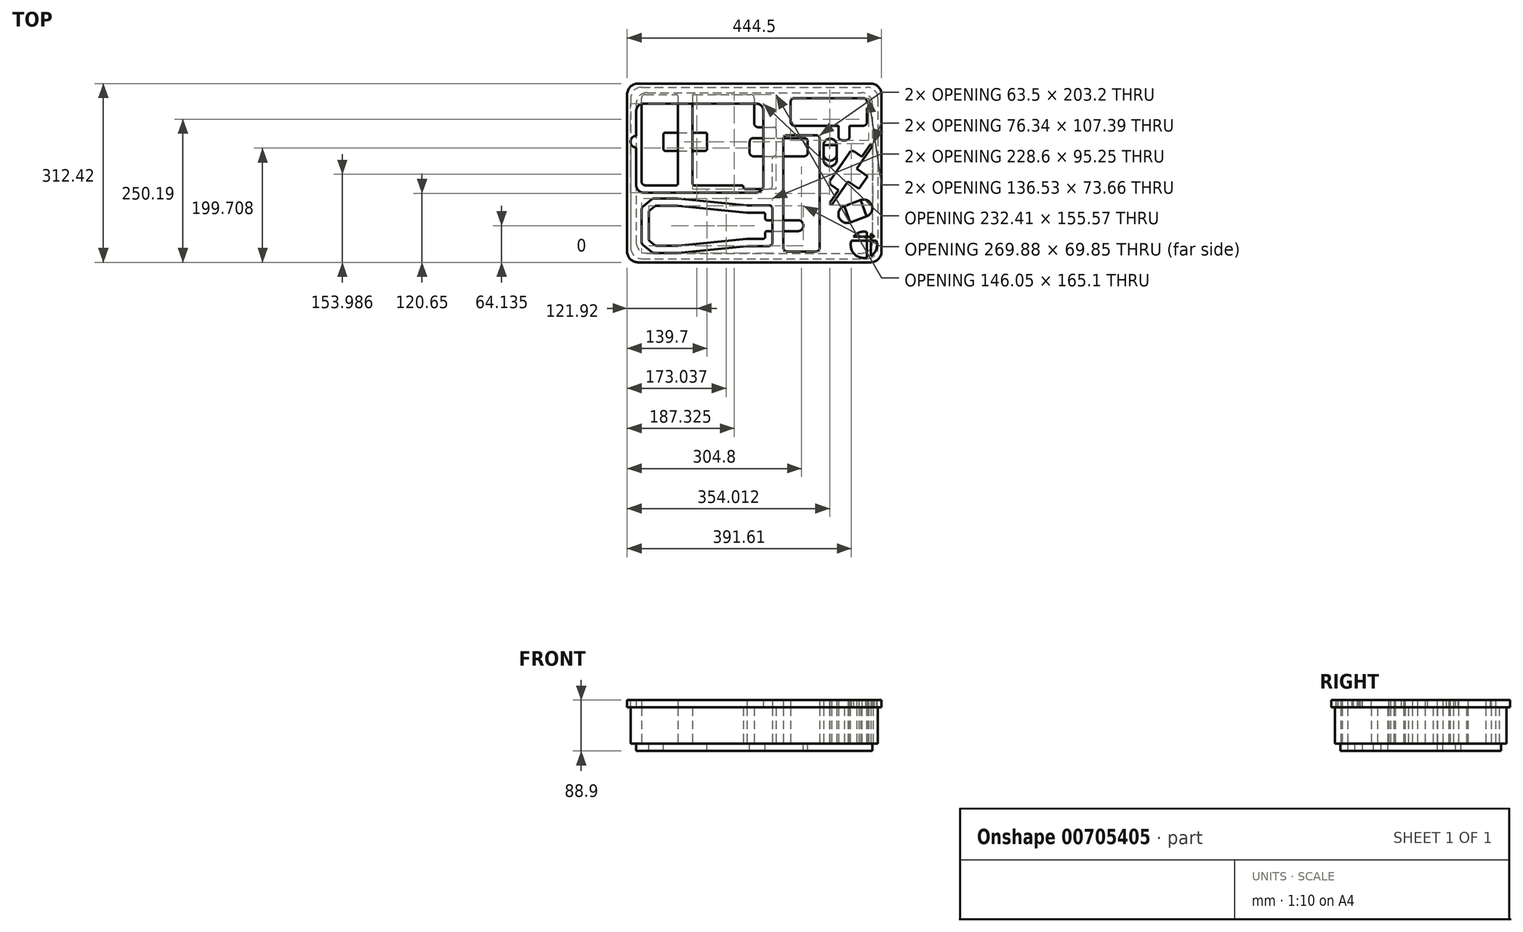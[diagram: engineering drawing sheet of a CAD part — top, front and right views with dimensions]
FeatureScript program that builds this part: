
annotation { "Feature Type Name" : "Feature", "Feature Type Description" : "" }
export const myFeature = defineFeature(function(context is Context, id is Id, definition is map)
    precondition{}
    {
        {
            var Q0;
            Q0=qCreatedBy(makeId("Top.planeOp"),FACE);
            var sketch = newSketch(context, id + "F0", { "sketchPlane" : qUnion([Q0])});
            skLineSegment(sketch, "E0.bottom", {"start": v(-196.85, 149.86) * mm, "end": v(196.85, 149.86) * mm});
            skLineSegment(sketch, "E0.top", {"start": v(-196.85, -149.86) * mm, "end": v(196.85, -149.86) * mm});
            skLineSegment(sketch, "E0.left", {"start": v(-215.9, 130.81) * mm, "end": v(-215.9, -130.81) * mm});
            skLineSegment(sketch, "E0.right", {"start": v(215.9, 130.81) * mm, "end": v(215.9, -130.8) * mm});
            skLineSegment(sketch, "E1.bottom", {"start": v(-196.85, -15.24) * mm, "end": v(-196.85, 130.81) * mm});
            skLineSegment(sketch, "E1.top", {"start": v(31.75, -21.59) * mm, "end": v(31.75, 26.04) * mm});
            skLineSegment(sketch, "E1.right", {"start": v(-190.5, 137.16) * mm, "end": v(-136.52, 137.16) * mm});
            skLineSegment(sketch, "E2.bottom", {"start": v(157, -57.85) * mm, "end": v(185.64, -47.43) * mm});
            skLineSegment(sketch, "E2.top", {"start": v(167.42, -86.5) * mm, "end": v(196.06, -76.07) * mm});
            skLineSegment(sketch, "E2.left", {"start": v(157, -57.85) * mm, "end": v(167.42, -86.5) * mm});
            skLineSegment(sketch, "E2.right", {"start": v(185.64, -47.43) * mm, "end": v(196.06, -76.07) * mm});
            skLineSegment(sketch, "E3", {"start": v(149.5, 11.49) * mm, "end": v(190.26, -16.66) * mm, "construction": true});
            skLineSegment(sketch, "E4", {"start": v(149.5, 11.49) * mm, "end": v(132.9, -12.55) * mm});
            skLineSegment(sketch, "E5", {"start": v(134.52, -21.38) * mm, "end": v(147.06, -30.04) * mm});
            skLineSegment(sketch, "E6", {"start": v(147.06, -30.04) * mm, "end": v(131.19, -53.04) * mm});
            skLineSegment(sketch, "E7", {"start": v(131.19, -53.04) * mm, "end": v(135.37, -55.92) * mm});
            skLineSegment(sketch, "E8", {"start": v(179.03, 7.3) * mm, "end": v(197.84, -5.68) * mm});
            skLineSegment(sketch, "E9", {"start": v(197.84, -5.68) * mm, "end": v(190.26, -16.66) * mm});
            skPoint(sketch, "E10.visualSharp", {"position": v(129.3, -17.78) * mm});
            skArc(sketch, "E10.filletArc", {"start": v(132.9, -12.55) * mm, "mid": v(131.89, -17.3) * mm, "end": v(134.52, -21.38) * mm});
            skArc(sketch, "E11.MirrorCS", {"start": v(166.1, 35.52) * mm, "mid": v(170.18, 38.16) * mm, "end": v(174.93, 37.14) * mm});
            skLineSegment(sketch, "E12.MirrorCS", {"start": v(187.47, 28.48) * mm, "end": v(203.35, 51.47) * mm});
            skLineSegment(sketch, "E13.MirrorCS", {"start": v(174.93, 37.14) * mm, "end": v(187.47, 28.48) * mm});
            skPoint(sketch, "E14.MirrorP", {"position": v(169.7, 40.75) * mm});
            skLineSegment(sketch, "E15.MirrorCS", {"start": v(163.87, -14.64) * mm, "end": v(182.68, -27.63) * mm});
            skLineSegment(sketch, "E16.MirrorCS", {"start": v(149.5, 11.49) * mm, "end": v(166.1, 35.52) * mm});
            skLineSegment(sketch, "E17.MirrorCS", {"start": v(182.68, -27.63) * mm, "end": v(190.26, -16.66) * mm});
            skLineSegment(sketch, "E18", {"start": v(163.87, -14.64) * mm, "end": v(135.37, -55.92) * mm});
            skPoint(sketch, "E19.visualSharp", {"position": v(-215.9, 149.86) * mm});
            skArc(sketch, "E19.filletArc", {"start": v(-196.85, 149.86) * mm, "mid": v(-210.32, 144.28) * mm, "end": v(-215.9, 130.81) * mm});
            skPoint(sketch, "E20.visualSharp", {"position": v(215.9, 149.86) * mm});
            skArc(sketch, "E20.filletArc", {"start": v(215.9, 130.81) * mm, "mid": v(210.32, 144.28) * mm, "end": v(196.85, 149.86) * mm});
            skPoint(sketch, "E21.visualSharp", {"position": v(215.9, -149.86) * mm});
            skArc(sketch, "E21.filletArc", {"start": v(196.85, -149.86) * mm, "mid": v(210.32, -144.28) * mm, "end": v(215.9, -130.8) * mm});
            skPoint(sketch, "E22.visualSharp", {"position": v(-215.9, -149.86) * mm});
            skArc(sketch, "E22.filletArc", {"start": v(-215.9, -130.81) * mm, "mid": v(-210.32, -144.28) * mm, "end": v(-196.85, -149.86) * mm});
            skPoint(sketch, "E23.visualSharp", {"position": v(-196.85, -27.94) * mm});
            skPoint(sketch, "E24.visualSharp", {"position": v(31.75, -27.94) * mm});
            skArc(sketch, "E24.filletArc", {"start": v(25.4, -27.94) * mm, "mid": v(29.9, -26.08) * mm, "end": v(31.75, -21.59) * mm});
            skPoint(sketch, "E25.visualSharp", {"position": v(-196.85, 137.16) * mm});
            skArc(sketch, "E25.filletArc", {"start": v(-190.5, 137.16) * mm, "mid": v(-195, 135.3) * mm, "end": v(-196.85, 130.81) * mm});
            skPoint(sketch, "E26.visualSharp", {"position": v(31.75, 137.16) * mm});
            skArc(sketch, "E26.filletArc", {"start": v(31.75, 130.81) * mm, "mid": v(29.9, 135.3) * mm, "end": v(25.4, 137.16) * mm, "construction": true});
            skLineSegment(sketch, "E27.bottom", {"start": v(63.5, 88.9) * mm, "end": v(63.5, 124.46) * mm});
            skLineSegment(sketch, "E27.top", {"start": v(196.85, 88.9) * mm, "end": v(196.85, 112.08) * mm});
            skLineSegment(sketch, "E27.left", {"start": v(69.85, 82.55) * mm, "end": v(146.05, 82.55) * mm});
            skLineSegment(sketch, "E27.right", {"start": v(69.85, 130.81) * mm, "end": v(190.5, 130.81) * mm});
            skLineSegment(sketch, "E28.bottom", {"start": v(147.32, 81.28) * mm, "end": v(147.32, 63.5) * mm});
            skLineSegment(sketch, "E28.top", {"start": v(166.37, 81.28) * mm, "end": v(166.37, 63.5) * mm});
            skLineSegment(sketch, "E28.right", {"start": v(153.67, 57.15) * mm, "end": v(160.02, 57.15) * mm});
            skLineSegment(sketch, "E29.trimOffspring", {"start": v(167.64, 82.55) * mm, "end": v(190.5, 82.55) * mm});
            skLineSegment(sketch, "E30", {"start": v(147.32, 82.55) * mm, "end": v(166.37, 82.55) * mm, "construction": true});
            skPoint(sketch, "E31.visualSharp", {"position": v(63.5, 82.55) * mm});
            skArc(sketch, "E31.filletArc", {"start": v(63.5, 88.9) * mm, "mid": v(65.36, 84.4) * mm, "end": v(69.85, 82.55) * mm});
            skPoint(sketch, "E32.visualSharp", {"position": v(196.85, 82.55) * mm});
            skArc(sketch, "E32.filletArc", {"start": v(190.5, 82.55) * mm, "mid": v(195, 84.4) * mm, "end": v(196.85, 88.9) * mm});
            skArc(sketch, "E33.filletArc", {"start": v(196.85, 124.46) * mm, "mid": v(195, 128.95) * mm, "end": v(190.5, 130.81) * mm});
            skPoint(sketch, "E34.visualSharp", {"position": v(63.5, 130.81) * mm});
            skArc(sketch, "E34.filletArc", {"start": v(69.85, 130.81) * mm, "mid": v(65.36, 128.95) * mm, "end": v(63.5, 124.46) * mm});
            skPoint(sketch, "E35.visualSharp", {"position": v(147.32, 57.15) * mm});
            skArc(sketch, "E35.filletArc", {"start": v(147.32, 63.5) * mm, "mid": v(149.18, 59) * mm, "end": v(153.67, 57.15) * mm});
            skPoint(sketch, "E36.visualSharp", {"position": v(166.37, 57.15) * mm});
            skArc(sketch, "E36.filletArc", {"start": v(160.02, 57.15) * mm, "mid": v(164.51, 59) * mm, "end": v(166.37, 63.5) * mm});
            skLineSegment(sketch, "E37.bottom", {"start": v(120.85, 48.4) * mm, "end": v(143.96, 48.4) * mm});
            skLineSegment(sketch, "E37.left", {"start": v(120.85, 48.4) * mm, "end": v(120.85, 33.17) * mm});
            skLineSegment(sketch, "E37.right", {"start": v(143.96, 48.4) * mm, "end": v(143.96, 33.17) * mm});
            skArc(sketch, "E38", {"start": v(120.85, 33.17) * mm, "mid": v(132.4, 21.6) * mm, "end": v(143.96, 33.17) * mm});
            skLineSegment(sketch, "E39.bottom", {"start": v(-196.85, -139.7) * mm, "end": v(-196.85, -44.45) * mm, "construction": true});
            skLineSegment(sketch, "E39.top", {"start": v(31.75, -139.7) * mm, "end": v(31.75, -44.45) * mm, "construction": true});
            skLineSegment(sketch, "E39.left", {"start": v(-196.85, -139.7) * mm, "end": v(31.75, -139.7) * mm, "construction": true});
            skLineSegment(sketch, "E39.right", {"start": v(-196.85, -44.45) * mm, "end": v(31.75, -44.45) * mm, "construction": true});
            skLineSegment(sketch, "E40", {"start": v(-196.85, -92.08) * mm, "end": v(31.75, -92.07) * mm, "construction": true});
            skLineSegment(sketch, "E41", {"start": v(-196.85, -123.83) * mm, "end": v(31.75, -123.82) * mm, "construction": true});
            skLineSegment(sketch, "E42.MirrorCS", {"start": v(-196.85, -60.33) * mm, "end": v(31.75, -60.32) * mm, "construction": true});
            skLineSegment(sketch, "E43", {"start": v(-196.85, -127.64) * mm, "end": v(31.75, -127.63) * mm, "construction": true});
            skLineSegment(sketch, "E44.MirrorCS", {"start": v(-196.85, -56.51) * mm, "end": v(31.75, -56.51) * mm, "construction": true});
            skLineSegment(sketch, "E45", {"start": v(-177.16, -139.7) * mm, "end": v(-177.16, -44.45) * mm, "construction": true});
            skLineSegment(sketch, "E46", {"start": v(-133.35, -139.7) * mm, "end": v(-133.35, -44.45) * mm, "construction": true});
            skLineSegment(sketch, "E47", {"start": v(-12.7, -139.7) * mm, "end": v(-12.7, -44.45) * mm, "construction": true});
            skLineSegment(sketch, "E48", {"start": v(-196.85, -120.79) * mm, "end": v(-196.85, -63.36) * mm});
            skLineSegment(sketch, "E49", {"start": v(-194.49, -58.42) * mm, "end": v(-178.9, -45.86) * mm});
            skLineSegment(sketch, "E50", {"start": v(-174.92, -44.45) * mm, "end": v(-133.35, -44.45) * mm});
            skLineSegment(sketch, "E51", {"start": v(-133.35, -44.45) * mm, "end": v(-12.7, -56.51) * mm});
            skLineSegment(sketch, "E52", {"start": v(-12.7, -56.51) * mm, "end": v(25.4, -56.51) * mm});
            skLineSegment(sketch, "E53", {"start": v(31.75, -62.86) * mm, "end": v(31.75, -121.28) * mm});
            skLineSegment(sketch, "E54", {"start": v(25.4, -127.63) * mm, "end": v(-12.7, -127.63) * mm});
            skLineSegment(sketch, "E55", {"start": v(-12.7, -127.64) * mm, "end": v(-133.35, -139.7) * mm});
            skLineSegment(sketch, "E56", {"start": v(-133.35, -139.7) * mm, "end": v(-174.92, -139.7) * mm});
            skLineSegment(sketch, "E57", {"start": v(-178.9, -138.3) * mm, "end": v(-194.49, -125.73) * mm});
            skPoint(sketch, "E58.visualSharp", {"position": v(31.75, -127.64) * mm});
            skArc(sketch, "E58.filletArc", {"start": v(25.4, -127.63) * mm, "mid": v(29.9, -125.78) * mm, "end": v(31.75, -121.28) * mm});
            skPoint(sketch, "E59.visualSharp", {"position": v(31.75, -56.51) * mm});
            skArc(sketch, "E59.filletArc", {"start": v(31.75, -62.86) * mm, "mid": v(29.9, -58.37) * mm, "end": v(25.4, -56.51) * mm});
            skPoint(sketch, "E60.visualSharp", {"position": v(-196.85, -123.83) * mm});
            skArc(sketch, "E60.filletArc", {"start": v(-196.85, -120.79) * mm, "mid": v(-196.23, -123.53) * mm, "end": v(-194.49, -125.73) * mm});
            skPoint(sketch, "E61.visualSharp", {"position": v(-177.16, -139.7) * mm});
            skArc(sketch, "E61.filletArc", {"start": v(-178.9, -138.3) * mm, "mid": v(-177.04, -139.34) * mm, "end": v(-174.92, -139.7) * mm});
            skPoint(sketch, "E62.visualSharp", {"position": v(-196.85, -60.33) * mm});
            skArc(sketch, "E62.filletArc", {"start": v(-194.49, -58.42) * mm, "mid": v(-196.23, -60.62) * mm, "end": v(-196.85, -63.36) * mm});
            skPoint(sketch, "E63.visualSharp", {"position": v(-177.16, -44.45) * mm});
            skArc(sketch, "E63.filletArc", {"start": v(-174.92, -44.45) * mm, "mid": v(-177.04, -44.81) * mm, "end": v(-178.9, -45.86) * mm});
            skLineSegment(sketch, "E64", {"start": v(120.85, 33.17) * mm, "end": v(143.96, 33.17) * mm, "construction": true});
            skLineSegment(sketch, "E65.MirrorCS", {"start": v(179.03, 7.3) * mm, "end": v(207.53, 48.59) * mm});
            skLineSegment(sketch, "E66.MirrorCS", {"start": v(203.35, 51.47) * mm, "end": v(207.53, 48.59) * mm});
            skLineSegment(sketch, "E67", {"start": v(198.12, 122.87) * mm, "end": v(198.76, 122.87) * mm});
            skLineSegment(sketch, "E68", {"start": v(200.02, 121.6) * mm, "end": v(200.02, 114.62) * mm});
            skLineSegment(sketch, "E69", {"start": v(198.76, 113.35) * mm, "end": v(198.12, 113.35) * mm});
            skPoint(sketch, "E70.visualSharp", {"position": v(166.37, 82.55) * mm});
            skArc(sketch, "E70.filletArc", {"start": v(167.64, 82.55) * mm, "mid": v(166.74, 82.18) * mm, "end": v(166.37, 81.28) * mm});
            skPoint(sketch, "E71.visualSharp", {"position": v(147.32, 82.55) * mm});
            skArc(sketch, "E71.filletArc", {"start": v(147.32, 81.28) * mm, "mid": v(146.95, 82.18) * mm, "end": v(146.05, 82.55) * mm});
            skPoint(sketch, "E72.visualSharp", {"position": v(200.03, 113.35) * mm});
            skArc(sketch, "E72.filletArc", {"start": v(198.76, 113.35) * mm, "mid": v(199.65, 113.72) * mm, "end": v(200.03, 114.62) * mm});
            skPoint(sketch, "E73.visualSharp", {"position": v(200.03, 122.87) * mm});
            skArc(sketch, "E73.filletArc", {"start": v(200.02, 121.6) * mm, "mid": v(199.65, 122.5) * mm, "end": v(198.76, 122.87) * mm});
            skPoint(sketch, "E74.visualSharp", {"position": v(196.85, 122.87) * mm});
            skArc(sketch, "E74.filletArc", {"start": v(196.85, 124.13) * mm, "mid": v(197.23, 123.24) * mm, "end": v(198.12, 122.87) * mm});
            skPoint(sketch, "E75.visualSharp", {"position": v(196.85, 113.35) * mm});
            skArc(sketch, "E75.filletArc", {"start": v(198.12, 113.35) * mm, "mid": v(197.22, 112.98) * mm, "end": v(196.85, 112.08) * mm});
            skLineSegment(sketch, "E76", {"start": v(-196.85, 54.61) * mm, "end": v(31.75, 54.61) * mm, "construction": true});
            skLineSegment(sketch, "E77", {"start": v(-82.55, -27.94) * mm, "end": v(-82.55, 137.16) * mm, "construction": true});
            skLineSegment(sketch, "E78", {"start": v(0, 149.86) * mm, "end": v(0, -149.86) * mm, "construction": true});
            skLineSegment(sketch, "E79", {"start": v(-215.9, 0) * mm, "end": v(215.9, 0) * mm, "construction": true});
            skPoint(sketch, "E80", {"position": v(0, 0) * mm});
            skPoint(sketch, "E81", {"position": v(-82.55, 54.61) * mm});
            skPoint(sketch, "E82", {"position": v(-133.35, -92.08) * mm});
            skLineSegment(sketch, "E83", {"start": v(63.5, 106.68) * mm, "end": v(196.85, 106.68) * mm, "construction": true});
            skLineSegment(sketch, "E84", {"start": v(130.18, 130.81) * mm, "end": v(130.18, 82.55) * mm, "construction": true});
            skPoint(sketch, "E85", {"position": v(130.18, 106.68) * mm});
            skLineSegment(sketch, "E86", {"start": v(163.87, -14.64) * mm, "end": v(179.03, 7.3) * mm, "construction": true});
            skPoint(sketch, "E87", {"position": v(171.45, -3.67) * mm});
            skLineSegment(sketch, "E88", {"start": v(196.85, 124.46) * mm, "end": v(196.85, 124.13) * mm});
            skLineSegment(sketch, "E89", {"start": v(196.85, 124.13) * mm, "end": v(196.85, 112.08) * mm, "construction": true});
            skArc(sketch, "E90", {"start": v(31.75, -21.59) * mm, "mid": v(29.9, -26.08) * mm, "end": v(25.4, -27.94) * mm});
            skLineSegment(sketch, "E91.bottom", {"start": v(107.95, -137.16) * mm, "end": v(57.15, -137.16) * mm});
            skLineSegment(sketch, "E91.top", {"start": v(107.95, 66.04) * mm, "end": v(57.15, 66.04) * mm});
            skLineSegment(sketch, "E91.left", {"start": v(114.3, -130.8) * mm, "end": v(114.3, 59.7) * mm});
            skLineSegment(sketch, "E91.right", {"start": v(50.8, -130.8) * mm, "end": v(50.8, 59.7) * mm});
            skLineSegment(sketch, "E92", {"start": v(82.55, -137.16) * mm, "end": v(82.55, 66.04) * mm, "construction": true});
            skLineSegment(sketch, "E93", {"start": v(114.3, -35.56) * mm, "end": v(50.8, -35.56) * mm, "construction": true});
            skPoint(sketch, "E94", {"position": v(82.55, -35.56) * mm});
            skPoint(sketch, "E95.visualSharp", {"position": v(114.3, -137.16) * mm});
            skArc(sketch, "E95.filletArc", {"start": v(107.95, -137.16) * mm, "mid": v(112.44, -135.3) * mm, "end": v(114.3, -130.8) * mm});
            skPoint(sketch, "E96.visualSharp", {"position": v(50.8, -137.16) * mm});
            skArc(sketch, "E96.filletArc", {"start": v(50.8, -130.8) * mm, "mid": v(52.66, -135.3) * mm, "end": v(57.15, -137.16) * mm});
            skPoint(sketch, "E97.visualSharp", {"position": v(50.8, 66.04) * mm});
            skArc(sketch, "E97.filletArc", {"start": v(57.15, 66.04) * mm, "mid": v(52.66, 64.18) * mm, "end": v(50.8, 59.7) * mm});
            skPoint(sketch, "E98.visualSharp", {"position": v(114.3, 66.04) * mm});
            skArc(sketch, "E98.filletArc", {"start": v(114.3, 59.7) * mm, "mid": v(112.44, 64.18) * mm, "end": v(107.95, 66.04) * mm});
            skLineSegment(sketch, "E99.left", {"start": v(-107.95, 133.99) * mm, "end": v(-107.95, -18.41) * mm});
            skLineSegment(sketch, "E99.right", {"start": v(-133.35, 133.99) * mm, "end": v(-133.35, -18.41) * mm});
            skLineSegment(sketch, "E100", {"start": v(34.93, 80.01) * mm, "end": v(34.92, 80.01) * mm});
            skLineSegment(sketch, "E101.MirrorCS", {"start": v(34.93, 29.21) * mm, "end": v(34.93, 29.21) * mm});
            skLineSegment(sketch, "E102", {"start": v(38.1, 76.84) * mm, "end": v(38.1, 32.39) * mm});
            skLineSegment(sketch, "E103", {"start": v(-104.77, 137.16) * mm, "end": v(-6.35, 137.16) * mm});
            skLineSegment(sketch, "E104", {"start": v(31.75, 83.19) * mm, "end": v(31.75, 130.81) * mm, "construction": true});
            skLineSegment(sketch, "E105", {"start": v(31.75, 29.21) * mm, "end": v(31.75, 80.01) * mm, "construction": true});
            skPoint(sketch, "E106.visualSharp", {"position": v(-107.95, 137.16) * mm});
            skArc(sketch, "E106.filletArc", {"start": v(-104.77, 137.16) * mm, "mid": v(-107.02, 136.23) * mm, "end": v(-107.95, 133.99) * mm});
            skPoint(sketch, "E107.visualSharp", {"position": v(-133.35, 137.16) * mm});
            skArc(sketch, "E107.filletArc", {"start": v(-133.35, 133.99) * mm, "mid": v(-134.28, 136.23) * mm, "end": v(-136.52, 137.16) * mm});
            skPoint(sketch, "E108.visualSharp", {"position": v(31.75, 80.01) * mm});
            skPoint(sketch, "E109.visualSharp", {"position": v(31.75, 29.21) * mm});
            skArc(sketch, "E109.filletArc", {"start": v(34.93, 29.21) * mm, "mid": v(32.68, 28.28) * mm, "end": v(31.75, 26.04) * mm});
            skPoint(sketch, "E110.visualSharp", {"position": v(38.1, 29.21) * mm});
            skArc(sketch, "E110.filletArc", {"start": v(34.93, 29.21) * mm, "mid": v(37.17, 30.14) * mm, "end": v(38.1, 32.39) * mm});
            skPoint(sketch, "E111.visualSharp", {"position": v(38.1, 80.01) * mm});
            skArc(sketch, "E111.filletArc", {"start": v(38.1, 76.84) * mm, "mid": v(37.17, 79.08) * mm, "end": v(34.92, 80.01) * mm});
            skLineSegment(sketch, "E112", {"start": v(0, 130.81) * mm, "end": v(0, 86.36) * mm});
            skLineSegment(sketch, "E113", {"start": v(6.35, 80.01) * mm, "end": v(34.93, 80.01) * mm});
            skPoint(sketch, "E114.visualSharp", {"position": v(0, 80.01) * mm});
            skArc(sketch, "E114.filletArc", {"start": v(0, 86.36) * mm, "mid": v(1.86, 81.87) * mm, "end": v(6.35, 80.01) * mm});
            skLineSegment(sketch, "E115", {"start": v(-6.35, 137.16) * mm, "end": v(0, 137.16) * mm, "construction": true});
            skLineSegment(sketch, "E116", {"start": v(0, 137.16) * mm, "end": v(25.4, 137.16) * mm, "construction": true});
            skPoint(sketch, "E117.visualSharp", {"position": v(0, 137.16) * mm});
            skArc(sketch, "E117.filletArc", {"start": v(0, 130.81) * mm, "mid": v(-1.86, 135.3) * mm, "end": v(-6.35, 137.16) * mm});
            skLineSegment(sketch, "E118", {"start": v(-6.35, 137.16) * mm, "end": v(-6.35, 137.16) * mm});
            skLineSegment(sketch, "E119", {"start": v(-19.05, -24.76) * mm, "end": v(-19.05, -24.76) * mm});
            skLineSegment(sketch, "E120", {"start": v(-22.22, -21.59) * mm, "end": v(-104.78, -21.59) * mm});
            skLineSegment(sketch, "E121", {"start": v(-133.35, -21.59) * mm, "end": v(-133.35, -24.76) * mm, "construction": true});
            skLineSegment(sketch, "E122", {"start": v(-15.88, -27.94) * mm, "end": v(25.4, -27.94) * mm});
            skLineSegment(sketch, "E123", {"start": v(-107.95, -21.59) * mm, "end": v(-107.95, -24.76) * mm, "construction": true});
            skPoint(sketch, "E124.visualSharp", {"position": v(-196.85, -21.59) * mm});
            skArc(sketch, "E124.filletArc", {"start": v(-196.85, -15.24) * mm, "mid": v(-195, -19.73) * mm, "end": v(-190.5, -21.59) * mm});
            skPoint(sketch, "E125.visualSharp", {"position": v(-19.05, -21.59) * mm});
            skArc(sketch, "E125.filletArc", {"start": v(-19.05, -24.76) * mm, "mid": v(-19.98, -22.52) * mm, "end": v(-22.22, -21.59) * mm});
            skPoint(sketch, "E126.visualSharp", {"position": v(-19.05, -27.94) * mm});
            skArc(sketch, "E126.filletArc", {"start": v(-19.05, -24.76) * mm, "mid": v(-18.12, -27.01) * mm, "end": v(-15.88, -27.94) * mm});
            skLineSegment(sketch, "E127", {"start": v(-136.53, -21.59) * mm, "end": v(-190.5, -21.59) * mm});
            skPoint(sketch, "E128.visualSharp", {"position": v(-133.35, -21.59) * mm});
            skArc(sketch, "E128.filletArc", {"start": v(-136.53, -21.59) * mm, "mid": v(-134.28, -20.66) * mm, "end": v(-133.35, -18.41) * mm});
            skPoint(sketch, "E129.visualSharp", {"position": v(-107.95, -21.59) * mm});
            skArc(sketch, "E129.filletArc", {"start": v(-107.95, -18.41) * mm, "mid": v(-107.02, -20.66) * mm, "end": v(-104.78, -21.59) * mm});
            skLineSegment(sketch, "E130", {"start": v(-136.53, -21.59) * mm, "end": v(-104.78, -21.59) * mm, "construction": true});
            skLineSegment(sketch, "E131", {"start": v(-136.52, 137.16) * mm, "end": v(-104.77, 137.16) * mm, "construction": true});
            skSolve(sketch);
        }
        {
            var Q0;
            Q0=qSketchRegion(id+"F0",true);
            extrude(context, id + "F1", {"entities" : qUnion([Q0]), "depth" : 63.5 * mm, "offsetDistance" : 25.4 * mm});
        }
        {
            var Q0;
            Q0=qCreatedBy(makeId("Top.planeOp"),FACE);
            var sketch = newSketch(context, id + "F2", { "sketchPlane" : qUnion([Q0])});
            skLineSegment(sketch, "E132.0", {"start": v(-215.9, 149.86) * mm, "end": v(215.9, 149.86) * mm, "construction": true});
            skLineSegment(sketch, "E133.0", {"start": v(-215.9, 149.86) * mm, "end": v(-215.9, -149.86) * mm, "construction": true});
            skLineSegment(sketch, "E134.0", {"start": v(215.9, 149.86) * mm, "end": v(215.9, -149.86) * mm, "construction": true});
            skLineSegment(sketch, "E135.0", {"start": v(-190.26, -149.86) * mm, "end": v(215.9, -149.86) * mm, "construction": true});
            skPoint(sketch, "E136.orphan", {"position": v(-196.85, 149.86) * mm});
            skPoint(sketch, "E137.orphan", {"position": v(-215.9, 130.81) * mm});
            skPoint(sketch, "E138.orphan", {"position": v(196.85, 149.86) * mm});
            skPoint(sketch, "E139.orphan", {"position": v(215.9, 130.81) * mm});
            skPoint(sketch, "E140.orphan", {"position": v(215.9, -130.8) * mm});
            skPoint(sketch, "E141.orphan", {"position": v(196.85, -149.86) * mm});
            skPoint(sketch, "E142.orphan", {"position": v(-196.85, -149.86) * mm});
            skPoint(sketch, "E143.orphan", {"position": v(-215.9, -130.81) * mm});
            skPoint(sketch, "E144", {"position": v(0, 0) * mm});
            skLineSegment(sketch, "E145", {"start": v(0, 149.86) * mm, "end": v(0, -149.86) * mm, "construction": true});
            skPoint(sketch, "E145.startSnap0", {"position": v(0, 149.86) * mm});
            skLineSegment(sketch, "E146", {"start": v(-215.9, 0) * mm, "end": v(215.9, 0) * mm, "construction": true});
            skLineSegment(sketch, "E147.bottom", {"start": v(-187.32, 140.34) * mm, "end": v(187.33, 140.34) * mm});
            skLineSegment(sketch, "E147.top", {"start": v(-187.33, -140.33) * mm, "end": v(187.32, -140.33) * mm});
            skLineSegment(sketch, "E147.left", {"start": v(-206.38, 121.29) * mm, "end": v(-206.38, -121.28) * mm});
            skLineSegment(sketch, "E147.right", {"start": v(206.38, 121.29) * mm, "end": v(206.38, -121.28) * mm});
            skPoint(sketch, "E148.visualSharp", {"position": v(-206.38, 140.34) * mm});
            skPoint(sketch, "E149.visualSharp", {"position": v(206.38, 140.34) * mm});
            skPoint(sketch, "E150.visualSharp", {"position": v(206.38, -140.33) * mm});
            skPoint(sketch, "E151.visualSharp", {"position": v(-206.38, -140.33) * mm});
            skLineSegment(sketch, "E152.0.0", {"start": v(-12.7, -127.63) * mm, "end": v(25.4, -127.63) * mm, "construction": true});
            skArc(sketch, "E152.0.1", {"start": v(25.4, -127.63) * mm, "mid": v(29.9, -125.78) * mm, "end": v(31.75, -121.28) * mm, "construction": true});
            skLineSegment(sketch, "E152.0.2", {"start": v(31.75, -121.28) * mm, "end": v(31.75, -62.86) * mm, "construction": true});
            skArc(sketch, "E152.0.3", {"start": v(31.75, -62.86) * mm, "mid": v(29.9, -58.37) * mm, "end": v(25.4, -56.51) * mm, "construction": true});
            skLineSegment(sketch, "E152.0.4", {"start": v(25.4, -56.51) * mm, "end": v(-12.7, -56.51) * mm, "construction": true});
            skLineSegment(sketch, "E152.0.5", {"start": v(-12.7, -56.52) * mm, "end": v(-133.35, -44.45) * mm, "construction": true});
            skLineSegment(sketch, "E152.0.6", {"start": v(-133.35, -44.45) * mm, "end": v(-174.92, -44.45) * mm, "construction": true});
            skArc(sketch, "E152.0.7", {"start": v(-174.92, -44.45) * mm, "mid": v(-177.04, -44.81) * mm, "end": v(-178.9, -45.86) * mm, "construction": true});
            skLineSegment(sketch, "E152.0.8", {"start": v(-178.9, -45.86) * mm, "end": v(-194.49, -58.42) * mm, "construction": true});
            skArc(sketch, "E152.0.9", {"start": v(-194.49, -58.42) * mm, "mid": v(-196.23, -60.62) * mm, "end": v(-196.85, -63.36) * mm, "construction": true});
            skLineSegment(sketch, "E152.0.10", {"start": v(-196.85, -63.36) * mm, "end": v(-196.85, -120.79) * mm, "construction": true});
            skArc(sketch, "E152.0.11", {"start": v(-196.85, -120.79) * mm, "mid": v(-196.23, -123.53) * mm, "end": v(-194.49, -125.73) * mm, "construction": true});
            skLineSegment(sketch, "E152.0.12", {"start": v(-194.49, -125.73) * mm, "end": v(-178.9, -138.3) * mm, "construction": true});
            skArc(sketch, "E152.0.13", {"start": v(-178.9, -138.3) * mm, "mid": v(-177.04, -139.34) * mm, "end": v(-174.92, -139.7) * mm, "construction": true});
            skLineSegment(sketch, "E152.0.14", {"start": v(-174.92, -139.7) * mm, "end": v(-133.35, -139.7) * mm, "construction": true});
            skLineSegment(sketch, "E152.0.15", {"start": v(-133.35, -139.7) * mm, "end": v(-12.7, -127.64) * mm, "construction": true});
            skArc(sketch, "E153.filletArc", {"start": v(-187.32, 140.34) * mm, "mid": v(-200.8, 134.76) * mm, "end": v(-206.38, 121.29) * mm});
            skArc(sketch, "E154.filletArc", {"start": v(206.38, 121.29) * mm, "mid": v(200.8, 134.76) * mm, "end": v(187.33, 140.34) * mm});
            skArc(sketch, "E155.filletArc", {"start": v(187.32, -140.33) * mm, "mid": v(200.8, -134.76) * mm, "end": v(206.37, -121.28) * mm});
            skArc(sketch, "E156.filletArc", {"start": v(-206.38, -121.28) * mm, "mid": v(-200.8, -134.76) * mm, "end": v(-187.33, -140.33) * mm});
            skLineSegment(sketch, "E157.0", {"start": v(-173.55, -57.85) * mm, "end": v(-182.97, -65.45) * mm});
            skLineSegment(sketch, "E157.1", {"start": v(-134.14, -57.15) * mm, "end": v(-171.56, -57.15) * mm});
            skLineSegment(sketch, "E157.2", {"start": v(-184.15, -67.92) * mm, "end": v(-184.15, -116.23) * mm});
            skLineSegment(sketch, "E157.3", {"start": v(-13.5, -69.2) * mm, "end": v(-133.83, -57.17) * mm});
            skLineSegment(sketch, "E157.4", {"start": v(15.88, -69.21) * mm, "end": v(-13.18, -69.21) * mm});
            skLineSegment(sketch, "E157.5", {"start": v(19.05, -111.76) * mm, "end": v(19.05, -104.78) * mm});
            skLineSegment(sketch, "E157.6", {"start": v(-182.97, -118.7) * mm, "end": v(-173.55, -126.3) * mm});
            skLineSegment(sketch, "E157.7", {"start": v(-171.56, -127) * mm, "end": v(-134.14, -127) * mm});
            skLineSegment(sketch, "E157.8", {"start": v(-133.83, -126.98) * mm, "end": v(-13.5, -114.95) * mm});
            skLineSegment(sketch, "E157.9", {"start": v(-13.18, -114.93) * mm, "end": v(15.88, -114.93) * mm});
            skLineSegment(sketch, "E158", {"start": v(22.23, -82.55) * mm, "end": v(76.2, -82.55) * mm});
            skLineSegment(sketch, "E159", {"start": v(-184.15, -92.08) * mm, "end": v(76.2, -92.08) * mm, "construction": true});
            skLineSegment(sketch, "E160", {"start": v(76.2, -82.55) * mm, "end": v(76.2, -92.08) * mm, "construction": true});
            skLineSegment(sketch, "E161.MirrorCS", {"start": v(22.23, -101.6) * mm, "end": v(76.2, -101.6) * mm});
            skLineSegment(sketch, "E162.MirrorCS", {"start": v(76.2, -101.6) * mm, "end": v(76.2, -92.08) * mm, "construction": true});
            skLineSegment(sketch, "E163", {"start": v(19.05, -79.37) * mm, "end": v(19.05, -72.39) * mm});
            skPoint(sketch, "E164.orphan", {"position": v(19.05, -92.08) * mm});
            skArc(sketch, "E165", {"start": v(76.2, -82.55) * mm, "mid": v(85.73, -92.08) * mm, "end": v(76.2, -101.6) * mm});
            skLineSegment(sketch, "E166.bottom", {"start": v(-1.78, 60.96) * mm, "end": v(87.12, 60.96) * mm});
            skLineSegment(sketch, "E166.top", {"start": v(-1.78, 29.21) * mm, "end": v(87.12, 29.21) * mm});
            skLineSegment(sketch, "E166.left", {"start": v(-8.13, 54.61) * mm, "end": v(-8.13, 35.56) * mm});
            skLineSegment(sketch, "E166.right", {"start": v(93.47, 54.61) * mm, "end": v(93.47, 35.56) * mm});
            skPoint(sketch, "E167.visualSharp", {"position": v(-8.13, 60.96) * mm});
            skArc(sketch, "E167.filletArc", {"start": v(-1.78, 60.96) * mm, "mid": v(-6.27, 59.1) * mm, "end": v(-8.13, 54.61) * mm});
            skPoint(sketch, "E168.visualSharp", {"position": v(93.47, 60.96) * mm});
            skArc(sketch, "E168.filletArc", {"start": v(93.47, 54.61) * mm, "mid": v(91.61, 59.1) * mm, "end": v(87.12, 60.96) * mm});
            skPoint(sketch, "E169.visualSharp", {"position": v(93.47, 29.21) * mm});
            skArc(sketch, "E169.filletArc", {"start": v(87.12, 29.21) * mm, "mid": v(91.61, 31.07) * mm, "end": v(93.47, 35.56) * mm});
            skPoint(sketch, "E170.visualSharp", {"position": v(-8.13, 29.21) * mm});
            skArc(sketch, "E170.filletArc", {"start": v(-8.13, 35.56) * mm, "mid": v(-6.27, 31.07) * mm, "end": v(-1.78, 29.21) * mm});
            skPoint(sketch, "E171.visualSharp", {"position": v(19.05, -69.21) * mm});
            skArc(sketch, "E171.filletArc", {"start": v(19.05, -72.39) * mm, "mid": v(18.12, -70.14) * mm, "end": v(15.88, -69.21) * mm});
            skPoint(sketch, "E172.visualSharp", {"position": v(19.05, -82.55) * mm});
            skArc(sketch, "E172.filletArc", {"start": v(19.05, -79.37) * mm, "mid": v(19.98, -81.62) * mm, "end": v(22.23, -82.55) * mm});
            skPoint(sketch, "E173.visualSharp", {"position": v(19.05, -101.6) * mm});
            skArc(sketch, "E173.filletArc", {"start": v(22.23, -101.6) * mm, "mid": v(19.98, -102.53) * mm, "end": v(19.05, -104.78) * mm});
            skPoint(sketch, "E174.visualSharp", {"position": v(19.05, -114.94) * mm});
            skArc(sketch, "E174.filletArc", {"start": v(15.88, -114.94) * mm, "mid": v(18.12, -114) * mm, "end": v(19.05, -111.76) * mm});
            skPoint(sketch, "E175.visualSharp", {"position": v(-184.15, -66.4) * mm});
            skArc(sketch, "E175.filletArc", {"start": v(-182.97, -65.45) * mm, "mid": v(-183.84, -66.55) * mm, "end": v(-184.15, -67.92) * mm});
            skPoint(sketch, "E176.visualSharp", {"position": v(-172.68, -57.15) * mm});
            skArc(sketch, "E176.filletArc", {"start": v(-171.56, -57.15) * mm, "mid": v(-172.62, -57.33) * mm, "end": v(-173.55, -57.85) * mm});
            skPoint(sketch, "E177.visualSharp", {"position": v(-133.98, -57.15) * mm});
            skArc(sketch, "E177.filletArc", {"start": v(-133.83, -57.17) * mm, "mid": v(-133.98, -57.15) * mm, "end": v(-134.14, -57.15) * mm});
            skPoint(sketch, "E178.visualSharp", {"position": v(-184.15, -117.75) * mm});
            skArc(sketch, "E178.filletArc", {"start": v(-184.15, -116.23) * mm, "mid": v(-183.84, -117.6) * mm, "end": v(-182.97, -118.7) * mm});
            skPoint(sketch, "E179.visualSharp", {"position": v(-172.68, -127) * mm});
            skArc(sketch, "E179.filletArc", {"start": v(-173.55, -126.3) * mm, "mid": v(-172.62, -126.82) * mm, "end": v(-171.56, -127) * mm});
            skPoint(sketch, "E180.visualSharp", {"position": v(-133.98, -127) * mm});
            skArc(sketch, "E180.filletArc", {"start": v(-134.14, -127) * mm, "mid": v(-133.98, -127) * mm, "end": v(-133.83, -126.98) * mm});
            skPoint(sketch, "E181.visualSharp", {"position": v(-13.33, -114.93) * mm});
            skArc(sketch, "E181.filletArc", {"start": v(-13.18, -114.93) * mm, "mid": v(-13.33, -114.94) * mm, "end": v(-13.5, -114.95) * mm});
            skPoint(sketch, "E182.visualSharp", {"position": v(-13.33, -69.21) * mm});
            skArc(sketch, "E182.filletArc", {"start": v(-13.5, -69.2) * mm, "mid": v(-13.33, -69.21) * mm, "end": v(-13.18, -69.21) * mm});
            skLineSegment(sketch, "E183.0", {"start": v(-196.85, 54.61) * mm, "end": v(31.75, 54.61) * mm, "construction": true});
            skLineSegment(sketch, "E184.0", {"start": v(-133.35, 133.99) * mm, "end": v(-133.35, -18.41) * mm, "construction": true});
            skLineSegment(sketch, "E185.0", {"start": v(-107.95, 133.99) * mm, "end": v(-107.95, -18.41) * mm, "construction": true});
            skLineSegment(sketch, "E186", {"start": v(-158.75, 54.61) * mm, "end": v(-158.75, 67.31) * mm});
            skLineSegment(sketch, "E187", {"start": v(-155.57, 70.49) * mm, "end": v(-85.72, 70.49) * mm});
            skLineSegment(sketch, "E188", {"start": v(-82.55, 67.31) * mm, "end": v(-82.55, 54.61) * mm});
            skLineSegment(sketch, "E189.MirrorCS", {"start": v(-82.55, 41.91) * mm, "end": v(-82.55, 54.61) * mm});
            skLineSegment(sketch, "E190.MirrorCS", {"start": v(-158.75, 54.61) * mm, "end": v(-158.75, 41.91) * mm});
            skLineSegment(sketch, "E191.MirrorCS", {"start": v(-155.57, 38.74) * mm, "end": v(-85.72, 38.74) * mm});
            skPoint(sketch, "E192.visualSharp", {"position": v(-158.75, 70.49) * mm});
            skArc(sketch, "E192.filletArc", {"start": v(-155.57, 70.49) * mm, "mid": v(-157.82, 69.56) * mm, "end": v(-158.75, 67.31) * mm});
            skPoint(sketch, "E193.visualSharp", {"position": v(-158.75, 38.74) * mm});
            skArc(sketch, "E193.filletArc", {"start": v(-158.75, 41.91) * mm, "mid": v(-157.82, 39.66) * mm, "end": v(-155.57, 38.74) * mm});
            skPoint(sketch, "E194.visualSharp", {"position": v(-82.55, 38.74) * mm});
            skArc(sketch, "E194.filletArc", {"start": v(-85.72, 38.74) * mm, "mid": v(-83.48, 39.66) * mm, "end": v(-82.55, 41.91) * mm});
            skPoint(sketch, "E195.visualSharp", {"position": v(-82.55, 70.49) * mm});
            skArc(sketch, "E195.filletArc", {"start": v(-82.55, 67.31) * mm, "mid": v(-83.48, 69.56) * mm, "end": v(-85.72, 70.49) * mm});
            skSolve(sketch);
        }
        {
            var Q0;
            Q0=qSketchRegion(id+"F2",true);
            extrude(context, id + "F3", {"entities" : qUnion([Q0]), "oppositeDirection" : true, "depth" : 12.7 * mm, "offsetDistance" : 25.4 * mm});
        }
        {
            var Q0;
            Q0=makeQuery(id+"F1.opExtrude","CAP_FACE",FACE,{"disambiguationData":[OSD([sQuery(id+"F0.wireOp",EDGE,"E0.bottom"),sQuery(id+"F0.wireOp",EDGE,"E0.top"),sQuery(id+"F0.wireOp",EDGE,"E0.left"),sQuery(id+"F0.wireOp",EDGE,"E0.right"),sQuery(id+"F0.wireOp",EDGE,"E1.bottom"),sQuery(id+"F0.wireOp",EDGE,"E1.top"),sQuery(id+"F0.wireOp",EDGE,"E1.left"),sQuery(id+"F0.wireOp",EDGE,"E1.right"),sQuery(id+"F0.wireOp",EDGE,"E2.bottom"),sQuery(id+"F0.wireOp",EDGE,"E2.top"),sQuery(id+"F0.wireOp",EDGE,"E2.left"),sQuery(id+"F0.wireOp",EDGE,"E2.right"),sQuery(id+"F0.wireOp",EDGE,"E4"),sQuery(id+"F0.wireOp",EDGE,"E5"),sQuery(id+"F0.wireOp",EDGE,"E6"),sQuery(id+"F0.wireOp",EDGE,"E7"),sQuery(id+"F0.wireOp",EDGE,"E8"),sQuery(id+"F0.wireOp",EDGE,"E9"),sQuery(id+"F0.wireOp",EDGE,"E10.filletArc"),sQuery(id+"F0.wireOp",EDGE,"E11.MirrorCS"),sQuery(id+"F0.wireOp",EDGE,"E12.MirrorCS"),sQuery(id+"F0.wireOp",EDGE,"E13.MirrorCS"),sQuery(id+"F0.wireOp",EDGE,"E15.MirrorCS"),sQuery(id+"F0.wireOp",EDGE,"E16.MirrorCS"),sQuery(id+"F0.wireOp",EDGE,"E17.MirrorCS"),sQuery(id+"F0.wireOp",EDGE,"E18"),sQuery(id+"F0.wireOp",EDGE,"E19.filletArc"),sQuery(id+"F0.wireOp",EDGE,"E20.filletArc"),sQuery(id+"F0.wireOp",EDGE,"E21.filletArc"),sQuery(id+"F0.wireOp",EDGE,"E22.filletArc"),sQuery(id+"F0.wireOp",EDGE,"E23.filletArc"),sQuery(id+"F0.wireOp",EDGE,"E25.filletArc"),sQuery(id+"F0.wireOp",EDGE,"E26.filletArc"),sQuery(id+"F0.wireOp",EDGE,"E27.bottom"),sQuery(id+"F0.wireOp",EDGE,"E27.top"),sQuery(id+"F0.wireOp",EDGE,"E27.left"),sQuery(id+"F0.wireOp",EDGE,"E27.right"),sQuery(id+"F0.wireOp",EDGE,"E28.bottom"),sQuery(id+"F0.wireOp",EDGE,"E28.top"),sQuery(id+"F0.wireOp",EDGE,"E28.right"),sQuery(id+"F0.wireOp",EDGE,"E29.trimOffspring"),sQuery(id+"F0.wireOp",EDGE,"E31.filletArc"),sQuery(id+"F0.wireOp",EDGE,"E32.filletArc"),sQuery(id+"F0.wireOp",EDGE,"E33.filletArc"),sQuery(id+"F0.wireOp",EDGE,"E34.filletArc"),sQuery(id+"F0.wireOp",EDGE,"E35.filletArc"),sQuery(id+"F0.wireOp",EDGE,"E36.filletArc"),sQuery(id+"F0.wireOp",EDGE,"E37.bottom"),sQuery(id+"F0.wireOp",EDGE,"E37.left"),sQuery(id+"F0.wireOp",EDGE,"E37.right"),sQuery(id+"F0.wireOp",EDGE,"E38"),sQuery(id+"F0.wireOp",EDGE,"E48"),sQuery(id+"F0.wireOp",EDGE,"E49"),sQuery(id+"F0.wireOp",EDGE,"E50"),sQuery(id+"F0.wireOp",EDGE,"E51"),sQuery(id+"F0.wireOp",EDGE,"E52"),sQuery(id+"F0.wireOp",EDGE,"E53"),sQuery(id+"F0.wireOp",EDGE,"E54"),sQuery(id+"F0.wireOp",EDGE,"E55"),sQuery(id+"F0.wireOp",EDGE,"E56"),sQuery(id+"F0.wireOp",EDGE,"E57"),sQuery(id+"F0.wireOp",EDGE,"E58.filletArc"),sQuery(id+"F0.wireOp",EDGE,"E59.filletArc"),sQuery(id+"F0.wireOp",EDGE,"E60.filletArc"),sQuery(id+"F0.wireOp",EDGE,"E61.filletArc"),sQuery(id+"F0.wireOp",EDGE,"E62.filletArc"),sQuery(id+"F0.wireOp",EDGE,"E63.filletArc"),sQuery(id+"F0.wireOp",EDGE,"E65.MirrorCS"),sQuery(id+"F0.wireOp",EDGE,"E66.MirrorCS"),sQuery(id+"F0.wireOp",EDGE,"E67"),sQuery(id+"F0.wireOp",EDGE,"E68"),sQuery(id+"F0.wireOp",EDGE,"E69"),sQuery(id+"F0.wireOp",EDGE,"E70.filletArc"),sQuery(id+"F0.wireOp",EDGE,"E71.filletArc"),sQuery(id+"F0.wireOp",EDGE,"E72.filletArc"),sQuery(id+"F0.wireOp",EDGE,"E73.filletArc"),sQuery(id+"F0.wireOp",EDGE,"E74.filletArc"),sQuery(id+"F0.wireOp",EDGE,"E75.filletArc"),sQuery(id+"F0.wireOp",EDGE,"E88"),sQuery(id+"F0.wireOp",EDGE,"E90"),sQuery(id+"F0.wireOp",EDGE,"E91.bottom"),sQuery(id+"F0.wireOp",EDGE,"E91.top"),sQuery(id+"F0.wireOp",EDGE,"E91.left"),sQuery(id+"F0.wireOp",EDGE,"E91.right"),sQuery(id+"F0.wireOp",EDGE,"E95.filletArc"),sQuery(id+"F0.wireOp",EDGE,"E96.filletArc"),sQuery(id+"F0.wireOp",EDGE,"E97.filletArc"),sQuery(id+"F0.wireOp",EDGE,"E98.filletArc")])],"isStart":false});
            var sketch = newSketch(context, id + "F4", { "sketchPlane" : qUnion([Q0])});
            skLineSegment(sketch, "E196.bottom", {"start": v(-203.2, 156.21) * mm, "end": v(203.2, 156.21) * mm});
            skLineSegment(sketch, "E196.top", {"start": v(-203.2, -156.2) * mm, "end": v(203.2, -156.2) * mm});
            skLineSegment(sketch, "E196.left", {"start": v(-222.25, 137.16) * mm, "end": v(-222.25, -137.16) * mm});
            skLineSegment(sketch, "E196.right", {"start": v(222.25, 137.16) * mm, "end": v(222.25, -137.16) * mm});
            skLineSegment(sketch, "E197.bottom", {"start": v(-196.85, -21.59) * mm, "end": v(-196.85, 130.81) * mm, "construction": true});
            skLineSegment(sketch, "E197.top", {"start": v(31.75, -21.59) * mm, "end": v(31.75, 130.81) * mm, "construction": true});
            skLineSegment(sketch, "E197.left", {"start": v(-190.5, -27.94) * mm, "end": v(25.4, -27.94) * mm, "construction": true});
            skLineSegment(sketch, "E197.right", {"start": v(-190.5, 137.16) * mm, "end": v(25.4, 137.16) * mm, "construction": true});
            skPoint(sketch, "E198.MirrorP", {"position": v(126.46, 6.88) * mm});
            skPoint(sketch, "E199.visualSharp", {"position": v(-222.25, 156.21) * mm});
            skArc(sketch, "E199.filletArc", {"start": v(-203.2, 156.21) * mm, "mid": v(-216.67, 150.63) * mm, "end": v(-222.25, 137.16) * mm});
            skPoint(sketch, "E200.visualSharp", {"position": v(222.25, 156.21) * mm});
            skArc(sketch, "E200.filletArc", {"start": v(222.25, 137.16) * mm, "mid": v(216.67, 150.63) * mm, "end": v(203.2, 156.21) * mm});
            skPoint(sketch, "E201.visualSharp", {"position": v(222.25, -156.2) * mm});
            skArc(sketch, "E201.filletArc", {"start": v(203.2, -156.2) * mm, "mid": v(216.67, -150.63) * mm, "end": v(222.25, -137.16) * mm});
            skPoint(sketch, "E202.visualSharp", {"position": v(-222.25, -156.2) * mm});
            skArc(sketch, "E202.filletArc", {"start": v(-222.25, -137.16) * mm, "mid": v(-216.67, -150.63) * mm, "end": v(-203.2, -156.21) * mm});
            skPoint(sketch, "E203.visualSharp", {"position": v(-196.85, -27.94) * mm});
            skArc(sketch, "E203.filletArc", {"start": v(-196.85, -21.59) * mm, "mid": v(-195, -26.08) * mm, "end": v(-190.5, -27.94) * mm, "construction": true});
            skPoint(sketch, "E204.visualSharp", {"position": v(31.75, -27.94) * mm});
            skArc(sketch, "E204.filletArc", {"start": v(25.4, -27.94) * mm, "mid": v(29.9, -26.08) * mm, "end": v(31.75, -21.59) * mm, "construction": true});
            skPoint(sketch, "E205.visualSharp", {"position": v(-196.85, 137.16) * mm});
            skArc(sketch, "E205.filletArc", {"start": v(-190.5, 137.16) * mm, "mid": v(-195, 135.3) * mm, "end": v(-196.85, 130.81) * mm, "construction": true});
            skPoint(sketch, "E206.visualSharp", {"position": v(31.75, 137.16) * mm});
            skArc(sketch, "E206.filletArc", {"start": v(31.75, 130.81) * mm, "mid": v(29.9, 135.3) * mm, "end": v(25.4, 137.16) * mm, "construction": true});
            skLineSegment(sketch, "E207.bottom", {"start": v(63.5, 88.9) * mm, "end": v(63.5, 124.46) * mm});
            skLineSegment(sketch, "E207.top", {"start": v(196.85, 88.9) * mm, "end": v(196.85, 112.08) * mm});
            skLineSegment(sketch, "E207.left", {"start": v(69.85, 82.55) * mm, "end": v(146.05, 82.55) * mm});
            skLineSegment(sketch, "E207.right", {"start": v(69.85, 130.81) * mm, "end": v(190.5, 130.81) * mm});
            skLineSegment(sketch, "E208.bottom", {"start": v(147.32, 81.28) * mm, "end": v(147.32, 63.5) * mm});
            skLineSegment(sketch, "E208.top", {"start": v(166.37, 81.28) * mm, "end": v(166.37, 63.5) * mm});
            skLineSegment(sketch, "E208.right", {"start": v(153.67, 57.15) * mm, "end": v(160.02, 57.15) * mm});
            skLineSegment(sketch, "E209.trimOffspring", {"start": v(167.64, 82.55) * mm, "end": v(190.5, 82.55) * mm});
            skLineSegment(sketch, "E210", {"start": v(147.32, 82.55) * mm, "end": v(166.37, 82.55) * mm, "construction": true});
            skPoint(sketch, "E211.visualSharp", {"position": v(63.5, 82.55) * mm});
            skArc(sketch, "E211.filletArc", {"start": v(63.5, 88.9) * mm, "mid": v(65.36, 84.4) * mm, "end": v(69.85, 82.55) * mm});
            skPoint(sketch, "E212.visualSharp", {"position": v(196.85, 82.55) * mm});
            skArc(sketch, "E212.filletArc", {"start": v(190.5, 82.55) * mm, "mid": v(195, 84.4) * mm, "end": v(196.85, 88.9) * mm});
            skPoint(sketch, "E213.visualSharp", {"position": v(196.85, 130.81) * mm});
            skArc(sketch, "E213.filletArc", {"start": v(196.85, 124.46) * mm, "mid": v(195, 128.95) * mm, "end": v(190.5, 130.81) * mm});
            skPoint(sketch, "E214.visualSharp", {"position": v(63.5, 130.81) * mm});
            skArc(sketch, "E214.filletArc", {"start": v(69.85, 130.81) * mm, "mid": v(65.36, 128.95) * mm, "end": v(63.5, 124.46) * mm});
            skPoint(sketch, "E215.visualSharp", {"position": v(147.32, 57.15) * mm});
            skArc(sketch, "E215.filletArc", {"start": v(147.32, 63.5) * mm, "mid": v(149.18, 59) * mm, "end": v(153.67, 57.15) * mm});
            skPoint(sketch, "E216.visualSharp", {"position": v(166.37, 57.15) * mm});
            skArc(sketch, "E216.filletArc", {"start": v(160.02, 57.15) * mm, "mid": v(164.51, 59) * mm, "end": v(166.37, 63.5) * mm});
            skLineSegment(sketch, "E217.bottom", {"start": v(120.85, 48.4) * mm, "end": v(143.96, 48.4) * mm, "construction": true});
            skLineSegment(sketch, "E217.left", {"start": v(120.85, 48.4) * mm, "end": v(120.85, 23) * mm});
            skLineSegment(sketch, "E217.right", {"start": v(143.96, 48.4) * mm, "end": v(143.96, 23) * mm});
            skArc(sketch, "E218", {"start": v(120.85, 23) * mm, "mid": v(132.4, 11.45) * mm, "end": v(143.96, 23) * mm});
            skLineSegment(sketch, "E219.bottom", {"start": v(-196.85, -139.7) * mm, "end": v(-196.85, -44.45) * mm, "construction": true});
            skLineSegment(sketch, "E219.top", {"start": v(31.75, -139.7) * mm, "end": v(31.75, -44.45) * mm, "construction": true});
            skLineSegment(sketch, "E219.left", {"start": v(-196.85, -139.7) * mm, "end": v(31.75, -139.7) * mm, "construction": true});
            skLineSegment(sketch, "E219.right", {"start": v(-196.85, -44.45) * mm, "end": v(31.75, -44.45) * mm, "construction": true});
            skLineSegment(sketch, "E220", {"start": v(-196.85, -92.07) * mm, "end": v(31.75, -92.07) * mm, "construction": true});
            skLineSegment(sketch, "E221", {"start": v(-196.85, -123.82) * mm, "end": v(31.75, -123.82) * mm, "construction": true});
            skLineSegment(sketch, "E222.MirrorCS", {"start": v(-196.85, -60.32) * mm, "end": v(31.75, -60.32) * mm, "construction": true});
            skLineSegment(sketch, "E223", {"start": v(-196.85, -127.63) * mm, "end": v(31.75, -127.63) * mm, "construction": true});
            skLineSegment(sketch, "E224.MirrorCS", {"start": v(-196.85, -56.51) * mm, "end": v(31.75, -56.51) * mm, "construction": true});
            skLineSegment(sketch, "E225", {"start": v(-177.16, -139.7) * mm, "end": v(-177.16, -44.45) * mm, "construction": true});
            skLineSegment(sketch, "E226", {"start": v(-133.35, -139.7) * mm, "end": v(-133.35, -44.45) * mm, "construction": true});
            skLineSegment(sketch, "E227", {"start": v(-12.7, -139.7) * mm, "end": v(-12.7, -44.45) * mm, "construction": true});
            skLineSegment(sketch, "E228", {"start": v(-196.85, -120.79) * mm, "end": v(-196.85, -63.36) * mm});
            skLineSegment(sketch, "E229", {"start": v(-194.49, -58.42) * mm, "end": v(-178.9, -45.86) * mm});
            skLineSegment(sketch, "E230", {"start": v(-174.92, -44.45) * mm, "end": v(-133.35, -44.45) * mm});
            skLineSegment(sketch, "E231", {"start": v(-133.35, -44.45) * mm, "end": v(-12.7, -56.51) * mm});
            skLineSegment(sketch, "E232", {"start": v(-12.7, -56.51) * mm, "end": v(25.4, -56.51) * mm});
            skLineSegment(sketch, "E233", {"start": v(31.75, -62.86) * mm, "end": v(31.75, -121.28) * mm});
            skLineSegment(sketch, "E234", {"start": v(25.4, -127.63) * mm, "end": v(-12.7, -127.63) * mm});
            skLineSegment(sketch, "E235", {"start": v(-12.7, -127.63) * mm, "end": v(-133.35, -139.7) * mm});
            skLineSegment(sketch, "E236", {"start": v(-133.35, -139.7) * mm, "end": v(-174.92, -139.7) * mm});
            skLineSegment(sketch, "E237", {"start": v(-178.9, -138.3) * mm, "end": v(-194.49, -125.73) * mm});
            skPoint(sketch, "E238.visualSharp", {"position": v(31.75, -127.63) * mm});
            skArc(sketch, "E238.filletArc", {"start": v(25.4, -127.63) * mm, "mid": v(29.9, -125.78) * mm, "end": v(31.75, -121.28) * mm});
            skPoint(sketch, "E239.visualSharp", {"position": v(31.75, -56.51) * mm});
            skArc(sketch, "E239.filletArc", {"start": v(31.75, -62.86) * mm, "mid": v(29.9, -58.37) * mm, "end": v(25.4, -56.51) * mm});
            skPoint(sketch, "E240.visualSharp", {"position": v(-196.85, -123.82) * mm});
            skArc(sketch, "E240.filletArc", {"start": v(-196.85, -120.79) * mm, "mid": v(-196.23, -123.53) * mm, "end": v(-194.49, -125.73) * mm});
            skPoint(sketch, "E241.visualSharp", {"position": v(-177.16, -139.7) * mm});
            skArc(sketch, "E241.filletArc", {"start": v(-178.9, -138.3) * mm, "mid": v(-177.04, -139.34) * mm, "end": v(-174.92, -139.7) * mm});
            skPoint(sketch, "E242.visualSharp", {"position": v(-196.85, -60.32) * mm});
            skArc(sketch, "E242.filletArc", {"start": v(-194.49, -58.42) * mm, "mid": v(-196.23, -60.62) * mm, "end": v(-196.85, -63.36) * mm});
            skPoint(sketch, "E243.visualSharp", {"position": v(-177.16, -44.45) * mm});
            skArc(sketch, "E243.filletArc", {"start": v(-174.92, -44.45) * mm, "mid": v(-177.04, -44.81) * mm, "end": v(-178.9, -45.86) * mm});
            skLineSegment(sketch, "E244", {"start": v(120.85, 23) * mm, "end": v(143.96, 23) * mm, "construction": true});
            skLineSegment(sketch, "E245", {"start": v(198.12, 122.87) * mm, "end": v(198.76, 122.87) * mm});
            skLineSegment(sketch, "E246", {"start": v(200.03, 121.6) * mm, "end": v(200.03, 114.62) * mm});
            skLineSegment(sketch, "E247", {"start": v(198.76, 113.35) * mm, "end": v(198.12, 113.35) * mm});
            skPoint(sketch, "E248.visualSharp", {"position": v(166.37, 82.55) * mm});
            skArc(sketch, "E248.filletArc", {"start": v(167.64, 82.55) * mm, "mid": v(166.74, 82.18) * mm, "end": v(166.37, 81.28) * mm});
            skPoint(sketch, "E249.visualSharp", {"position": v(147.32, 82.55) * mm});
            skArc(sketch, "E249.filletArc", {"start": v(147.32, 81.28) * mm, "mid": v(146.95, 82.18) * mm, "end": v(146.05, 82.55) * mm});
            skPoint(sketch, "E250.visualSharp", {"position": v(200.03, 113.35) * mm});
            skArc(sketch, "E250.filletArc", {"start": v(198.76, 113.35) * mm, "mid": v(199.65, 113.72) * mm, "end": v(200.03, 114.62) * mm});
            skPoint(sketch, "E251.visualSharp", {"position": v(200.03, 122.87) * mm});
            skArc(sketch, "E251.filletArc", {"start": v(200.03, 121.6) * mm, "mid": v(199.65, 122.5) * mm, "end": v(198.76, 122.87) * mm});
            skPoint(sketch, "E252.visualSharp", {"position": v(196.85, 122.87) * mm});
            skArc(sketch, "E252.filletArc", {"start": v(196.85, 124.13) * mm, "mid": v(197.23, 123.24) * mm, "end": v(198.12, 122.87) * mm});
            skPoint(sketch, "E253.visualSharp", {"position": v(196.85, 113.35) * mm});
            skArc(sketch, "E253.filletArc", {"start": v(198.12, 113.35) * mm, "mid": v(197.22, 112.98) * mm, "end": v(196.85, 112.08) * mm});
            skLineSegment(sketch, "E254", {"start": v(-196.85, 54.61) * mm, "end": v(31.75, 54.61) * mm, "construction": true});
            skLineSegment(sketch, "E255", {"start": v(-82.55, -27.94) * mm, "end": v(-82.55, 137.16) * mm, "construction": true});
            skLineSegment(sketch, "E256", {"start": v(0, 156.21) * mm, "end": v(0, -156.2) * mm, "construction": true});
            skLineSegment(sketch, "E257", {"start": v(-222.25, 0) * mm, "end": v(222.25, 0) * mm, "construction": true});
            skPoint(sketch, "E258", {"position": v(0, 0) * mm});
            skPoint(sketch, "E259", {"position": v(-82.55, 54.61) * mm});
            skPoint(sketch, "E260", {"position": v(-133.35, -92.07) * mm});
            skLineSegment(sketch, "E261", {"start": v(63.5, 106.68) * mm, "end": v(196.85, 106.68) * mm, "construction": true});
            skLineSegment(sketch, "E262", {"start": v(130.18, 130.81) * mm, "end": v(130.18, 82.55) * mm, "construction": true});
            skPoint(sketch, "E263", {"position": v(130.18, 106.68) * mm});
            skPoint(sketch, "E264", {"position": v(166.37, -12.7) * mm});
            skLineSegment(sketch, "E265", {"start": v(196.85, 124.46) * mm, "end": v(196.85, 124.13) * mm});
            skLineSegment(sketch, "E266", {"start": v(196.85, 124.13) * mm, "end": v(196.85, 112.08) * mm, "construction": true});
            skArc(sketch, "E267", {"start": v(31.75, -21.59) * mm, "mid": v(29.9, -26.08) * mm, "end": v(25.4, -27.94) * mm, "construction": true});
            skLineSegment(sketch, "E268.bottom", {"start": v(107.95, -137.16) * mm, "end": v(57.15, -137.16) * mm});
            skLineSegment(sketch, "E268.top", {"start": v(107.95, 66.04) * mm, "end": v(57.15, 66.04) * mm});
            skLineSegment(sketch, "E268.left", {"start": v(114.3, -130.8) * mm, "end": v(114.3, 59.69) * mm});
            skLineSegment(sketch, "E268.right", {"start": v(50.8, -130.8) * mm, "end": v(50.8, 59.69) * mm});
            skLineSegment(sketch, "E269", {"start": v(82.55, -137.16) * mm, "end": v(82.55, 66.04) * mm, "construction": true});
            skLineSegment(sketch, "E270", {"start": v(114.3, -35.56) * mm, "end": v(50.8, -35.56) * mm, "construction": true});
            skPoint(sketch, "E271", {"position": v(82.55, -35.56) * mm});
            skPoint(sketch, "E272.visualSharp", {"position": v(114.3, -137.16) * mm});
            skArc(sketch, "E272.filletArc", {"start": v(107.95, -137.16) * mm, "mid": v(112.44, -135.3) * mm, "end": v(114.3, -130.8) * mm});
            skPoint(sketch, "E273.visualSharp", {"position": v(50.8, -137.16) * mm});
            skArc(sketch, "E273.filletArc", {"start": v(50.8, -130.8) * mm, "mid": v(52.66, -135.3) * mm, "end": v(57.15, -137.16) * mm});
            skPoint(sketch, "E274.visualSharp", {"position": v(50.8, 66.04) * mm});
            skArc(sketch, "E274.filletArc", {"start": v(57.15, 66.04) * mm, "mid": v(52.66, 64.18) * mm, "end": v(50.8, 59.69) * mm});
            skPoint(sketch, "E275.visualSharp", {"position": v(114.3, 66.04) * mm});
            skArc(sketch, "E275.filletArc", {"start": v(114.3, 59.69) * mm, "mid": v(112.44, 64.18) * mm, "end": v(107.95, 66.04) * mm});
            skLineSegment(sketch, "E276", {"start": v(132.4, 48.4) * mm, "end": v(132.4, 11.45) * mm, "construction": true});
            skLineSegment(sketch, "E277.bottom", {"start": v(-193.68, 143.5) * mm, "end": v(-193.68, 143.5) * mm});
            skLineSegment(sketch, "E277.top", {"start": v(-193.68, -34.3) * mm, "end": v(3.17, -34.3) * mm});
            skLineSegment(sketch, "E277.left", {"start": v(-206.38, 130.8) * mm, "end": v(-206.38, 130.8) * mm});
            skLineSegment(sketch, "E277.right", {"start": v(41.28, 130.8) * mm, "end": v(41.28, 121.33) * mm, "construction": true});
            skPoint(sketch, "E278.visualSharp", {"position": v(-206.38, 143.5) * mm});
            skArc(sketch, "E278.filletArc", {"start": v(-193.68, 143.5) * mm, "mid": v(-202.66, 139.8) * mm, "end": v(-206.38, 130.8) * mm});
            skPoint(sketch, "E279.visualSharp", {"position": v(41.28, 143.5) * mm});
            skArc(sketch, "E279.filletArc", {"start": v(41.28, 130.8) * mm, "mid": v(37.56, 139.8) * mm, "end": v(28.58, 143.51) * mm});
            skPoint(sketch, "E280.visualSharp", {"position": v(41.27, -34.3) * mm});
            skArc(sketch, "E280.filletArc", {"start": v(28.57, -34.3) * mm, "mid": v(37.56, -30.57) * mm, "end": v(41.27, -21.6) * mm});
            skPoint(sketch, "E281.visualSharp", {"position": v(-206.38, -34.3) * mm});
            skArc(sketch, "E281.filletArc", {"start": v(-206.38, -21.6) * mm, "mid": v(-202.66, -30.57) * mm, "end": v(-193.68, -34.3) * mm});
            skArc(sketch, "E282", {"start": v(-206.38, 64.77) * mm, "mid": v(-216.54, 54.6) * mm, "end": v(-206.38, 44.45) * mm});
            skLineSegment(sketch, "E283", {"start": v(-206.38, 64.77) * mm, "end": v(-206.38, 44.45) * mm, "construction": true});
            skLineSegment(sketch, "E284", {"start": v(-206.38, 44.45) * mm, "end": v(-206.38, -21.6) * mm});
            skArc(sketch, "E285", {"start": v(120.85, 48.4) * mm, "mid": v(132.4, 59.96) * mm, "end": v(143.96, 48.4) * mm});
            skLineSegment(sketch, "E286", {"start": v(-193.68, 121.28) * mm, "end": v(3.18, 121.28) * mm});
            skLineSegment(sketch, "E287", {"start": v(15.88, 108.58) * mm, "end": v(15.87, -21.6) * mm});
            skPoint(sketch, "E288.visualSharp", {"position": v(15.88, 121.28) * mm});
            skArc(sketch, "E288.filletArc", {"start": v(15.88, 108.58) * mm, "mid": v(12.16, 117.57) * mm, "end": v(3.18, 121.28) * mm});
            skLineSegment(sketch, "E289", {"start": v(-206.38, 108.58) * mm, "end": v(-206.38, 64.77) * mm});
            skLineSegment(sketch, "E290", {"start": v(15.87, -34.3) * mm, "end": v(19, -34.3) * mm});
            skPoint(sketch, "E291.visualSharp", {"position": v(-206.38, 121.28) * mm});
            skArc(sketch, "E291.filletArc", {"start": v(-193.68, 121.28) * mm, "mid": v(-202.66, 117.57) * mm, "end": v(-206.38, 108.58) * mm});
            skPoint(sketch, "E292.visualSharp", {"position": v(15.87, -34.3) * mm});
            skArc(sketch, "E292.filletArc", {"start": v(3.17, -34.3) * mm, "mid": v(12.16, -30.57) * mm, "end": v(15.87, -21.6) * mm});
            skLineSegment(sketch, "E293", {"start": v(-206.38, 121.28) * mm, "end": v(-206.38, 110.32) * mm});
            skLineSegment(sketch, "E294", {"start": v(15.87, -34.3) * mm, "end": v(11.1, -34.3) * mm});
            skLineSegment(sketch, "E295", {"start": v(120.85, 33.17) * mm, "end": v(143.96, 33.17) * mm});
            skPoint(sketch, "E296", {"position": v(-206.38, 110.3) * mm});
            skPoint(sketch, "E297", {"position": v(-184.15, 143.5) * mm});
            skPoint(sketch, "E298", {"position": v(-158.75, 143.5) * mm});
            skPoint(sketch, "E299", {"position": v(-149.23, 143.5) * mm});
            skPoint(sketch, "E300", {"position": v(-123.83, 143.5) * mm});
            skPoint(sketch, "E301", {"position": v(-114.3, 143.5) * mm});
            skPoint(sketch, "E302", {"position": v(-88.9, 143.5) * mm});
            skPoint(sketch, "E303", {"position": v(-79.38, 143.5) * mm});
            skPoint(sketch, "E304", {"position": v(-53.97, 143.5) * mm});
            skPoint(sketch, "E305", {"position": v(-44.45, 143.5) * mm});
            skPoint(sketch, "E306", {"position": v(-19.05, 143.5) * mm});
            skPoint(sketch, "E307", {"position": v(-9.52, 143.5) * mm});
            skPoint(sketch, "E308", {"position": v(19.05, 143.5) * mm});
            skPoint(sketch, "E309", {"position": v(41.28, 121.28) * mm});
            skPoint(sketch, "E310", {"position": v(41.28, 95.88) * mm});
            skPoint(sketch, "E311", {"position": v(41.28, 86.36) * mm});
            skPoint(sketch, "E312", {"position": v(41.27, 60.96) * mm});
            skPoint(sketch, "E313", {"position": v(41.28, 51.43) * mm});
            skPoint(sketch, "E314", {"position": v(41.28, 54.6) * mm});
            skPoint(sketch, "E315", {"position": v(41.27, 26.03) * mm});
            skPoint(sketch, "E316", {"position": v(41.27, 16.5) * mm});
            skPoint(sketch, "E317", {"position": v(41.27, -12.07) * mm});
            skPoint(sketch, "E318", {"position": v(19.05, -34.3) * mm});
            skPoint(sketch, "E319", {"position": v(11.23, -34.3) * mm});
            skPoint(sketch, "E320", {"position": v(-206.38, 103.96) * mm});
            skPoint(sketch, "E321", {"position": v(4.88, -34.3) * mm});
            skLineSegment(sketch, "E322", {"start": v(-206.38, 110.32) * mm, "end": v(-206.38, 103.95) * mm, "construction": true});
            skLineSegment(sketch, "E323", {"start": v(-206.38, 108.58) * mm, "end": v(-206.38, 103.95) * mm});
            skLineSegment(sketch, "E324", {"start": v(-206.38, 130.8) * mm, "end": v(-206.38, 126.05) * mm, "construction": true});
            skLineSegment(sketch, "E325", {"start": v(-193.68, 143.5) * mm, "end": v(-184.33, 143.5) * mm, "construction": true});
            skLineSegment(sketch, "E326", {"start": v(-184.33, 143.5) * mm, "end": v(-158.7, 143.5) * mm});
            skLineSegment(sketch, "E327", {"start": v(-149.24, 143.5) * mm, "end": v(-123.98, 143.5) * mm});
            skLineSegment(sketch, "E328", {"start": v(-123.98, 143.5) * mm, "end": v(-114.26, 143.5) * mm, "construction": true});
            skLineSegment(sketch, "E329", {"start": v(-88.83, 143.5) * mm, "end": v(-79.25, 143.5) * mm, "construction": true});
            skLineSegment(sketch, "E330", {"start": v(-53.9, 143.5) * mm, "end": v(-44.37, 143.5) * mm, "construction": true});
            skLineSegment(sketch, "E331", {"start": v(-18.87, 143.5) * mm, "end": v(-9.66, 143.5) * mm, "construction": true});
            skLineSegment(sketch, "E332", {"start": v(-9.66, 143.5) * mm, "end": v(19.21, 143.5) * mm});
            skLineSegment(sketch, "E333", {"start": v(41.28, 121.33) * mm, "end": v(41.28, 96.14) * mm});
            skLineSegment(sketch, "E334", {"start": v(41.28, 96.14) * mm, "end": v(41.28, 86.93) * mm, "construction": true});
            skLineSegment(sketch, "E335", {"start": v(41.28, 86.93) * mm, "end": v(41.28, 61.3) * mm});
            skLineSegment(sketch, "E336", {"start": v(41.28, 61.3) * mm, "end": v(41.28, 51.84) * mm, "construction": true});
            skLineSegment(sketch, "E337", {"start": v(41.28, 51.84) * mm, "end": v(41.27, 26.06) * mm});
            skLineSegment(sketch, "E338", {"start": v(41.27, 26.06) * mm, "end": v(41.27, 16.63) * mm, "construction": true});
            skLineSegment(sketch, "E339", {"start": v(41.27, 16.63) * mm, "end": v(41.27, -11.65) * mm});
            skLineSegment(sketch, "E340", {"start": v(41.27, -11.65) * mm, "end": v(41.27, -21.6) * mm, "construction": true});
            skLineSegment(sketch, "E341", {"start": v(19, -34.3) * mm, "end": v(28.57, -34.3) * mm, "construction": true});
            skLineSegment(sketch, "E342", {"start": v(4.85, -34.3) * mm, "end": v(3.17, -34.3) * mm});
            skLineSegment(sketch, "E343", {"start": v(11.1, -34.3) * mm, "end": v(4.85, -34.3) * mm, "construction": true});
            skLineSegment(sketch, "E344", {"start": v(-158.7, 143.5) * mm, "end": v(-149.24, 143.5) * mm, "construction": true});
            skLineSegment(sketch, "E345", {"start": v(-114.26, 143.5) * mm, "end": v(-88.83, 143.5) * mm});
            skLineSegment(sketch, "E346", {"start": v(-79.25, 143.5) * mm, "end": v(-53.9, 143.5) * mm});
            skLineSegment(sketch, "E347", {"start": v(-44.37, 143.5) * mm, "end": v(-18.87, 143.5) * mm});
            skLineSegment(sketch, "E348", {"start": v(19.21, 143.5) * mm, "end": v(28.58, 143.5) * mm, "construction": true});
            skLineSegment(sketch, "E349", {"start": v(-206.38, 126.05) * mm, "end": v(-206.38, 121.28) * mm});
            skPoint(sketch, "E350.first.point", {"position": v(175.89, -108.6) * mm});
            skPoint(sketch, "E350.second.point", {"position": v(214.3, -123.2) * mm});
            skCircle(sketch, "E351", {"center": v(199.94, -114.77) * mm, "radius": 3.63 * mm});
            skPoint(sketch, "E351.first.point", {"position": v(196.76, -113.02) * mm});
            skPoint(sketch, "E351.second.point", {"position": v(202.03, -111.8) * mm});
            skPoint(sketch, "E351.third.point", {"position": v(200.4, -118.36) * mm});
            skPoint(sketch, "E352.first.point", {"position": v(194.7, -110.35) * mm});
            skPoint(sketch, "E352.second.point", {"position": v(204.98, -110.17) * mm});
            skPoint(sketch, "E352.third.point", {"position": v(204.24, -120) * mm});
            skLineSegment(sketch, "E353", {"start": v(173.4, -111.27) * mm, "end": v(194.05, -111.27) * mm});
            skLineSegment(sketch, "E354", {"start": v(169.62, -118.17) * mm, "end": v(194.04, -118.17) * mm});
            skLineSegment(sketch, "E355", {"start": v(203.48, -145.21) * mm, "end": v(203.48, -120.54) * mm});
            skArc(sketch, "E356", {"start": v(209.4, -111.27) * mm, "mid": v(206.67, -108.4) * mm, "end": v(203.48, -106.02) * mm});
            skLineSegment(sketch, "E357", {"start": v(205.8, -111.27) * mm, "end": v(209.4, -111.27) * mm});
            skLineSegment(sketch, "E358", {"start": v(203.48, -108.92) * mm, "end": v(203.48, -106.02) * mm});
            skArc(sketch, "E359", {"start": v(205.8, -111.27) * mm, "mid": v(204.78, -109.95) * mm, "end": v(203.48, -108.92) * mm});
            skArc(sketch, "E360", {"start": v(203.48, -120.54) * mm, "mid": v(204.79, -119.5) * mm, "end": v(205.8, -118.17) * mm});
            skArc(sketch, "E361", {"start": v(194.04, -118.17) * mm, "mid": v(195.13, -119.57) * mm, "end": v(196.53, -120.64) * mm});
            skArc(sketch, "E362", {"start": v(196.53, -108.82) * mm, "mid": v(195.13, -109.88) * mm, "end": v(194.05, -111.27) * mm});
            skLineSegment(sketch, "E363", {"start": v(196.53, -108.82) * mm, "end": v(196.53, -103.18) * mm});
            skLineSegment(sketch, "E364", {"start": v(205.8, -118.17) * mm, "end": v(213.18, -118.17) * mm});
            skArc(sketch, "E365", {"start": v(196.53, -103.18) * mm, "mid": v(183.8, -103.89) * mm, "end": v(173.4, -111.27) * mm});
            skArc(sketch, "E366", {"start": v(169.62, -118.17) * mm, "mid": v(174.3, -141.02) * mm, "end": v(196.53, -148.06) * mm});
            skLineSegment(sketch, "E367", {"start": v(196.53, -148.06) * mm, "end": v(196.53, -120.64) * mm});
            skArc(sketch, "E368", {"start": v(203.48, -145.21) * mm, "mid": v(213.07, -133.4) * mm, "end": v(213.18, -118.17) * mm});
            skLineSegment(sketch, "E369.0", {"start": v(157, -57.85) * mm, "end": v(185.64, -47.43) * mm});
            skLineSegment(sketch, "E370.0", {"start": v(157, -57.85) * mm, "end": v(167.42, -86.5) * mm});
            skLineSegment(sketch, "E371.0", {"start": v(167.42, -86.5) * mm, "end": v(196.06, -76.07) * mm});
            skPoint(sketch, "E372.0", {"position": v(190.85, -61.75) * mm});
            skLineSegment(sketch, "E373.0", {"start": v(185.64, -47.43) * mm, "end": v(196.06, -76.07) * mm});
            skLineSegment(sketch, "E374.0", {"start": v(166.1, 35.52) * mm, "end": v(132.9, -12.55) * mm});
            skPoint(sketch, "E375.0", {"position": v(131.89, -17.3) * mm});
            skLineSegment(sketch, "E376.0", {"start": v(134.52, -21.38) * mm, "end": v(147.06, -30.04) * mm});
            skLineSegment(sketch, "E377.0", {"start": v(147.06, -30.04) * mm, "end": v(131.19, -53.04) * mm});
            skLineSegment(sketch, "E378.0", {"start": v(131.19, -53.04) * mm, "end": v(135.37, -55.92) * mm});
            skArc(sketch, "E379.0", {"start": v(132.9, -12.55) * mm, "mid": v(131.89, -17.3) * mm, "end": v(134.52, -21.38) * mm});
            skLineSegment(sketch, "E380.0", {"start": v(163.87, -14.64) * mm, "end": v(135.37, -55.92) * mm});
            skLineSegment(sketch, "E381.0", {"start": v(163.87, -14.64) * mm, "end": v(182.68, -27.63) * mm});
            skLineSegment(sketch, "E382.0", {"start": v(197.84, -5.68) * mm, "end": v(182.68, -27.63) * mm});
            skLineSegment(sketch, "E383.0", {"start": v(179.03, 7.3) * mm, "end": v(197.84, -5.68) * mm});
            skLineSegment(sketch, "E384.0", {"start": v(179.03, 7.3) * mm, "end": v(207.53, 48.59) * mm});
            skLineSegment(sketch, "E385.0", {"start": v(203.35, 51.47) * mm, "end": v(207.53, 48.59) * mm});
            skLineSegment(sketch, "E386.0", {"start": v(187.47, 28.48) * mm, "end": v(203.35, 51.47) * mm});
            skLineSegment(sketch, "E387.0", {"start": v(174.93, 37.14) * mm, "end": v(187.47, 28.48) * mm});
            skArc(sketch, "E388.0", {"start": v(166.1, 35.52) * mm, "mid": v(170.18, 38.16) * mm, "end": v(174.93, 37.14) * mm});
            skArc(sketch, "E389", {"start": v(196.06, -76.07) * mm, "mid": v(205.17, -56.54) * mm, "end": v(185.64, -47.43) * mm});
            skArc(sketch, "E390", {"start": v(157, -57.85) * mm, "mid": v(147.89, -77.39) * mm, "end": v(167.42, -86.5) * mm});
            skSolve(sketch);
        }
        {
            var Q0;
            Q0=qSketchRegion(id+"F4",true);
            extrude(context, id + "F5", {"entities" : qUnion([Q0]), "depth" : 12.7 * mm, "offsetDistance" : 25.4 * mm});
        }
    });
